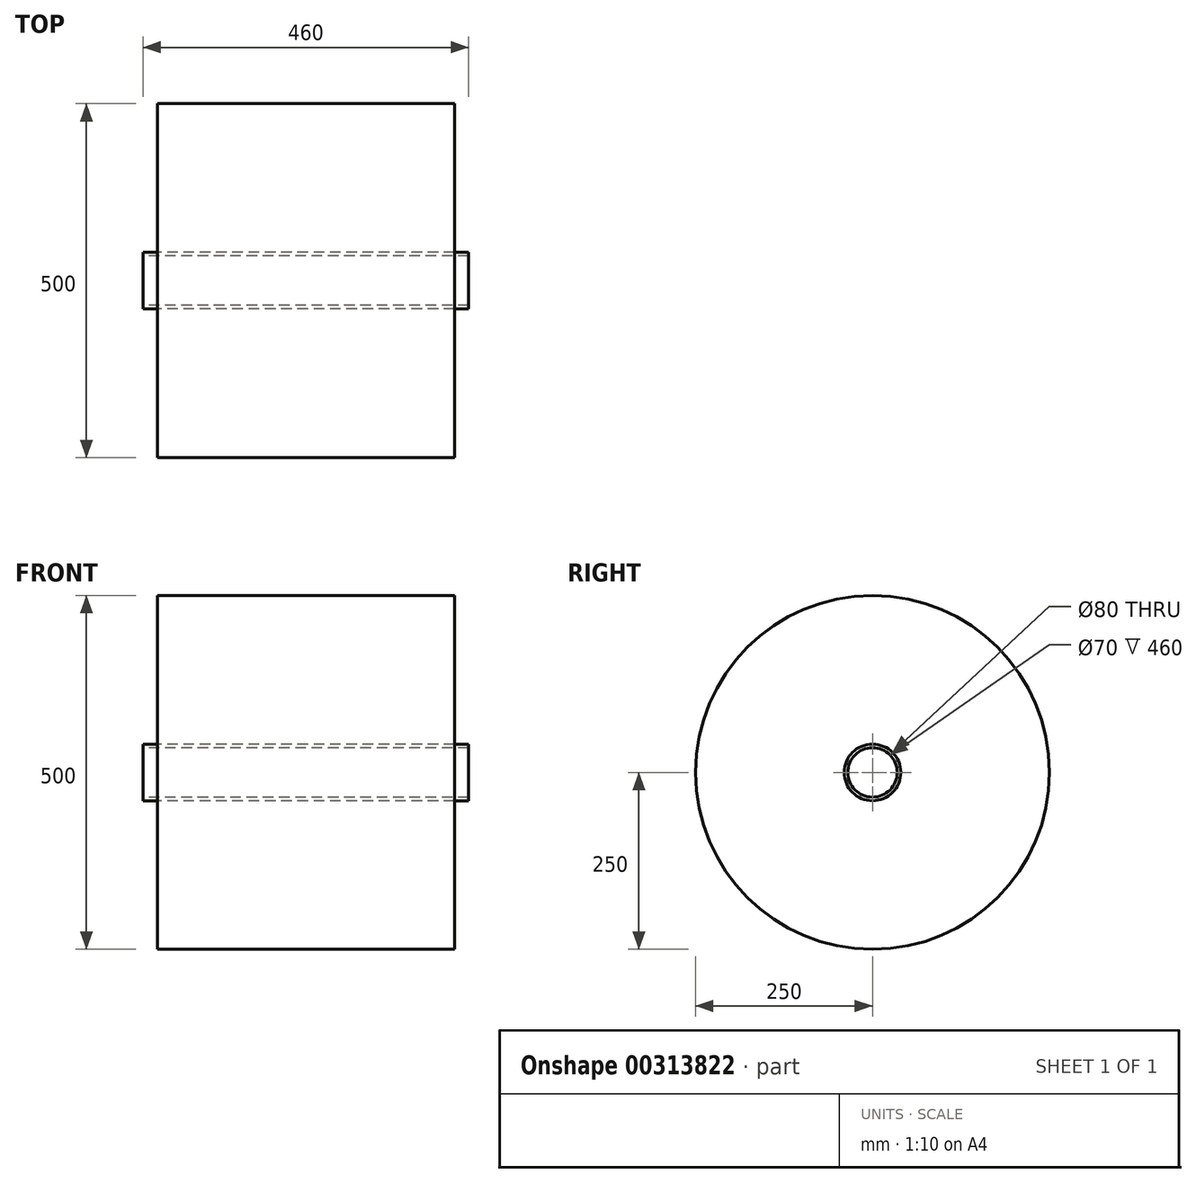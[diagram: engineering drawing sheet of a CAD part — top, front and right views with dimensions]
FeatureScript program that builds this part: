
annotation { "Feature Type Name" : "Feature", "Feature Type Description" : "" }
export const myFeature = defineFeature(function(context is Context, id is Id, definition is map)
    precondition{}
    {
        {
            var Q0;
            Q0=qCreatedBy(makeId("Right.planeOp"),FACE);
            var sketch = newSketch(context, id + "F0", { "sketchPlane" : qUnion([Q0])});
            skCircle(sketch, "E0", {"center": v(0, 0) * mm, "radius": 35 * mm});
            skCircle(sketch, "E1", {"center": v(0, 0) * mm, "radius": 40 * mm});
            skSolve(sketch);
        }
        {
            var Q0;
            Q0=makeQuery(id+"F0.imprint","IMPRINT",FACE,{"disambiguationData":[TD([[makeQuery(id+"F0.imprint","IMPRINT",EDGE,{"derivedFrom":sQuery(id+"F0.wireOp",EDGE,"E0")}),-1.0]])]});
            extrude(context, id + "F1", {"entities" : qUnion([Q0]), "endBound" : BoundingType.SYMMETRIC, "depth" : 460 * mm});
        }
        {
            var Q0;
            Q0=qCreatedBy(makeId("Right.planeOp"),FACE);
            var sketch = newSketch(context, id + "F2", { "sketchPlane" : qUnion([Q0])});
            skCircle(sketch, "E2", {"center": v(0, 0) * mm, "radius": 40 * mm});
            skCircle(sketch, "E3", {"center": v(0, 0) * mm, "radius": 250 * mm});
            skSolve(sketch);
        }
        {
            var Q0;
            Q0=makeQuery(id+"F2.imprint","IMPRINT",FACE,{"disambiguationData":[TD([[makeQuery(id+"F2.imprint","IMPRINT",EDGE,{"derivedFrom":sQuery(id+"F2.wireOp",EDGE,"E2")}),-1.0]])]});
            extrude(context, id + "F3", {"entities" : qUnion([Q0]), "endBound" : BoundingType.SYMMETRIC, "depth" : 420 * mm});
        }
    });
